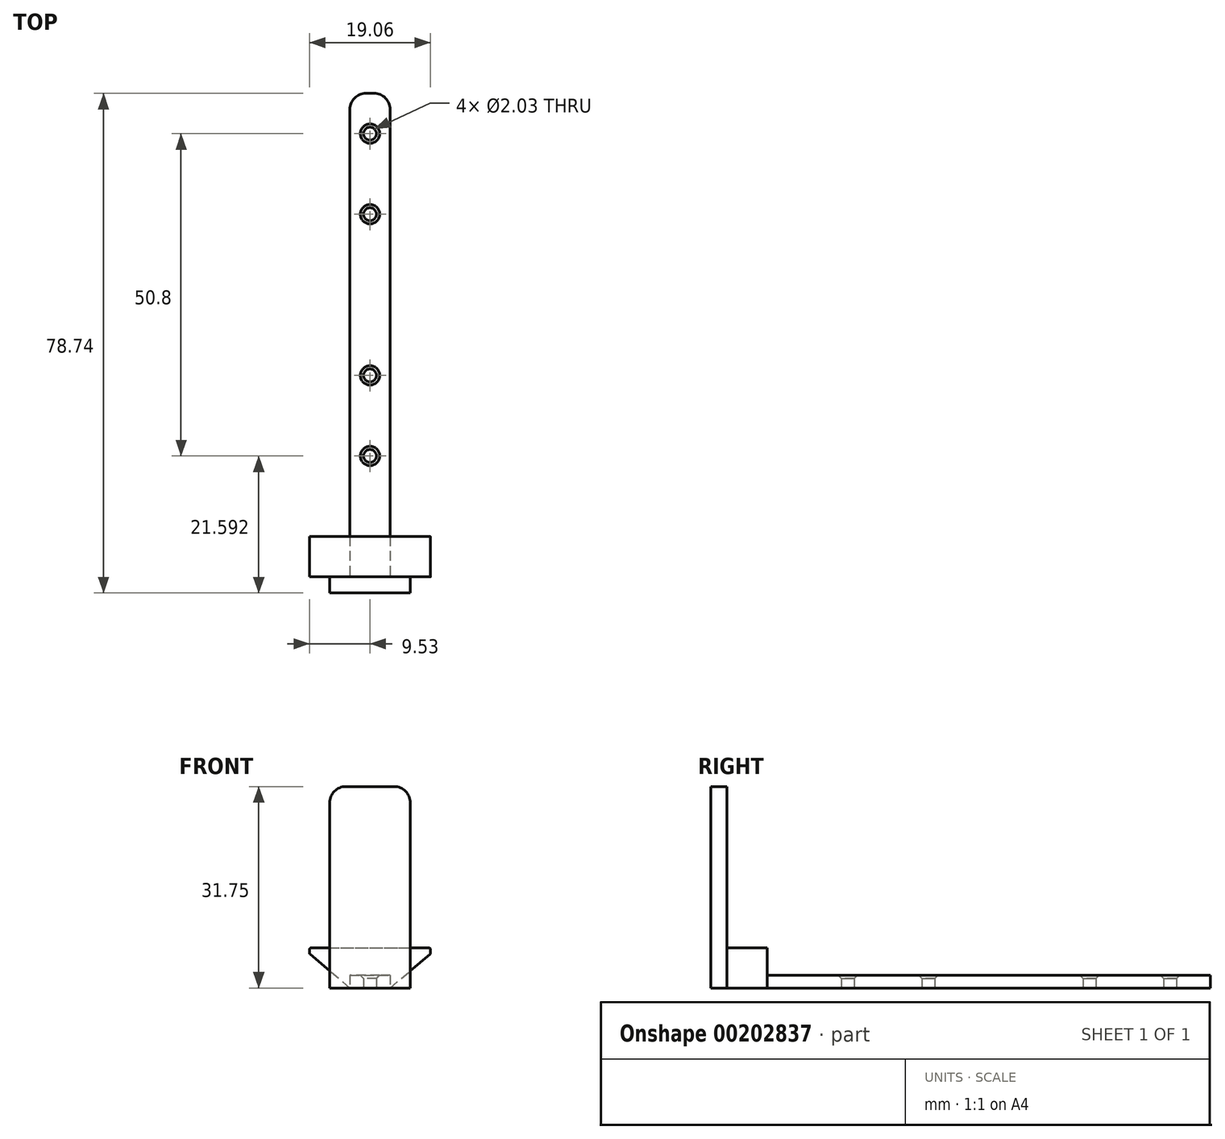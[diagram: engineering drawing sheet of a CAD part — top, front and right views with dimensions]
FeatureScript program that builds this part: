
annotation { "Feature Type Name" : "Feature", "Feature Type Description" : "" }
export const myFeature = defineFeature(function(context is Context, id is Id, definition is map)
    precondition{}
    {
        {
            var Q0;
            Q0=qCreatedBy(makeId("Top.planeOp"),FACE);
            var sketch = newSketch(context, id + "F0", { "sketchPlane" : qUnion([Q0])});
            skLineSegment(sketch, "E0.bottom", {"start": v(-3.18, 67.1) * mm, "end": v(3.18, 67.1) * mm});
            skLineSegment(sketch, "E0.top", {"start": v(-3.18, -9.1) * mm, "end": v(3.18, -9.1) * mm});
            skLineSegment(sketch, "E0.left", {"start": v(-3.18, 67.1) * mm, "end": v(-3.18, -9.1) * mm});
            skLineSegment(sketch, "E0.right", {"start": v(3.18, 67.1) * mm, "end": v(3.18, -9.1) * mm});
            skCircle(sketch, "E1", {"center": v(0, 9.94) * mm, "radius": 1.02 * mm});
            skCircle(sketch, "E2", {"center": v(0, 22.64) * mm, "radius": 1.02 * mm});
            skCircle(sketch, "E3", {"center": v(0, 48.04) * mm, "radius": 1.02 * mm});
            skCircle(sketch, "E4", {"center": v(0, 60.74) * mm, "radius": 1.02 * mm});
            skSolve(sketch);
        }
        {
            var Q0;
            Q0=makeQuery(id+"F0.imprint","IMPRINT",FACE,{"disambiguationData":[TD([[makeQuery(id+"F0.imprint","IMPRINT",EDGE,{"derivedFrom":sQuery(id+"F0.wireOp",EDGE,"E0.bottom")}),-1.0]])]});
            extrude(context, id + "F1", {"entities" : qUnion([Q0]), "depth" : 2.03 * mm});
        }
        {
            var Q0;
            Q0=makeQuery(id+"F1.opExtrude","SWEPT_FACE",FACE,{"disambiguationData":[OSD([sQuery(id+"F0.wireOp",EDGE,"E0.top")])]});
            var sketch = newSketch(context, id + "F2", { "sketchPlane" : qUnion([Q0])});
            skPoint(sketch, "E5.oppositeSnap0", {"position": v(3.17, 1.02) * mm});
            skLineSegment(sketch, "E5.bottom", {"start": v(-3.18, 0) * mm, "end": v(3.17, 0) * mm});
            skLineSegment(sketch, "E5.top", {"start": v(-3.18, 6.35) * mm, "end": v(3.17, 6.35) * mm});
            skLineSegment(sketch, "E6", {"start": v(3.18, 0) * mm, "end": v(9.52, 5.36) * mm});
            skLineSegment(sketch, "E7", {"start": v(-3.18, 0) * mm, "end": v(-9.52, 5.39) * mm});
            skLineSegment(sketch, "E8", {"start": v(-9.53, 6.35) * mm, "end": v(-9.53, 5.39) * mm});
            skLineSegment(sketch, "E9", {"start": v(9.52, 6.35) * mm, "end": v(9.52, 5.36) * mm});
            skLineSegment(sketch, "E10", {"start": v(-9.53, 6.35) * mm, "end": v(9.52, 6.35) * mm});
            skSolve(sketch);
        }
        {
            var Q0;
            Q0 = qSketchRegion(id + "F2", true);
            extrude(context, id + "F3", {"entities" : qUnion([Q0]), "operationType" : NewBodyOperationType.ADD, "oppositeDirection" : true, "depth" : 6.35 * mm});
        }
        {
            var Q0;
            Q0=makeQuery(id+"F3.opExtrude","SWEPT_EDGE",EDGE,{"disambiguationData":[OSD([sQuery(id+"F2.wireOp",EDGE,"E9"),sQuery(id+"F2.wireOp",EDGE,"E10")])]});
            fillet(context, id + "F4", {"entities" : qUnion([Q0]), "radius" : 0.25 * mm, "tangentPropagation" : true, "allowEdgeOverflow" : false});
        }
        {
            var Q0;
            Q0=makeQuery(id+"F3.opExtrude","SWEPT_EDGE",EDGE,{"disambiguationData":[OSD([sQuery(id+"F2.wireOp",EDGE,"E6"),sQuery(id+"F2.wireOp",EDGE,"E9")])]});
            var Q1;
            Q1=makeQuery(id+"F3.opExtrude","SWEPT_EDGE",EDGE,{"disambiguationData":[OSD([sQuery(id+"F2.wireOp",EDGE,"E8"),sQuery(id+"F2.wireOp",EDGE,"E10")])]});
            var Q2;
            Q2=makeQuery(id+"F3.opExtrude","SWEPT_EDGE",EDGE,{"disambiguationData":[OSD([sQuery(id+"F2.wireOp",EDGE,"E7"),sQuery(id+"F2.wireOp",EDGE,"E8")])]});
            fillet(context, id + "F5", {"entities" : qUnion([Q0, Q1, Q2]), "radius" : 0.25 * mm, "tangentPropagation" : true, "allowEdgeOverflow" : false});
        }
        {
            var Q0;
            Q0=makeQuery(id+"F1.opExtrude","CAP_EDGE",EDGE,{"disambiguationData":[OSD([sQuery(id+"F0.wireOp",EDGE,"E4")])],"isStart":false});
            chamfer(context, id + "F6", {"entities" : qUnion([Q0]), "width" : 0.5 * mm, "tangentPropagation" : true});
        }
        {
            var Q0;
            Q0=makeQuery(id+"F1.opExtrude","CAP_EDGE",EDGE,{"disambiguationData":[OSD([sQuery(id+"F0.wireOp",EDGE,"E3")])],"isStart":false});
            var Q1;
            Q1=makeQuery(id+"F1.opExtrude","CAP_EDGE",EDGE,{"disambiguationData":[OSD([sQuery(id+"F0.wireOp",EDGE,"E2")])],"isStart":false});
            var Q2;
            Q2=makeQuery(id+"F1.opExtrude","CAP_EDGE",EDGE,{"disambiguationData":[OSD([sQuery(id+"F0.wireOp",EDGE,"E1")])],"isStart":false});
            chamfer(context, id + "F7", {"entities" : qUnion([Q0, Q1, Q2]), "width" : 0.5 * mm, "tangentPropagation" : true});
        }
        {
            var Q0;
            Q0=makeQuery(id+"F3.boolean.opBoolean","MERGE",FACE,{"derivedFrom":[makeQuery(id+"F1.opExtrude","SWEPT_FACE",FACE,{"disambiguationData":[OSD([sQuery(id+"F0.wireOp",EDGE,"E0.top")])]}),makeQuery(id+"F3.opExtrude","CAP_FACE",FACE,{"disambiguationData":[OSD([sQuery(id+"F2.wireOp",EDGE,"E5.bottom"),sQuery(id+"F2.wireOp",EDGE,"E6"),sQuery(id+"F2.wireOp",EDGE,"E7"),sQuery(id+"F2.wireOp",EDGE,"E8"),sQuery(id+"F2.wireOp",EDGE,"E9"),sQuery(id+"F2.wireOp",EDGE,"E10")])],"isStart":true})]});
            var sketch = newSketch(context, id + "F8", { "sketchPlane" : qUnion([Q0])});
            skLineSegment(sketch, "E11.bottom", {"start": v(-6.35, 31.75) * mm, "end": v(6.35, 31.75) * mm});
            skLineSegment(sketch, "E11.top", {"start": v(-6.35, 0) * mm, "end": v(6.35, 0) * mm});
            skLineSegment(sketch, "E11.left", {"start": v(-6.35, 31.75) * mm, "end": v(-6.35, 0) * mm});
            skLineSegment(sketch, "E11.right", {"start": v(6.35, 31.75) * mm, "end": v(6.35, 0) * mm});
            skSolve(sketch);
        }
        {
            var Q0;
            {var subQ0=sQuery(id+"F8.wireOp",EDGE,"E11.bottom");Q0=makeQuery(id+"F8.imprint","IMPRINT",FACE,{"disambiguationData":[TD([[makeQuery(id+"F8.imprint","IMPRINT",EDGE,{"derivedFrom":subQ0}),-1.0]])]});}
            var Q1;
            {var subQ5=sQuery(id+"F8.wireOp",EDGE,"E11.top");var subQ9=makeQuery(id+"F3.opExtrude","CAP_EDGE",EDGE,{"disambiguationData":[OSD([sQuery(id+"F2.wireOp",EDGE,"E7")])],"isStart":true});var subQ11=makeQuery(id+"F8.imprint","INTERSECT",VERTEX,{"derivedFrom":[subQ9,subQ5]});Q1=makeQuery(id+"F8.imprint","IMPRINT",FACE,{"disambiguationData":[TD([[makeQuery(id+"F8.imprint","IMPRINT",EDGE,{"disambiguationData":[TD([[subQ11,-1.0]])],"derivedFrom":subQ5}),1.0]])]});}
            var Q2;
            {var subQ0=sQuery(id+"F8.wireOp",EDGE,"E11.top");var subQ1=makeQuery(id+"F3.opExtrude","CAP_EDGE",EDGE,{"disambiguationData":[OSD([sQuery(id+"F2.wireOp",EDGE,"E6")])],"isStart":true});var subQ2=makeQuery(id+"F8.imprint","INTERSECT",VERTEX,{"derivedFrom":[subQ1,subQ0]});Q2=makeQuery(id+"F8.imprint","IMPRINT",FACE,{"disambiguationData":[TD([[makeQuery(id+"F8.imprint","IMPRINT",EDGE,{"disambiguationData":[TD([[subQ2,-1.0]])],"derivedFrom":subQ0}),1.0]])]});}
            var Q3;
            {var subQ0=sQuery(id+"F8.wireOp",EDGE,"E11.top");var subQ1=makeQuery(id+"F3.opExtrude","CAP_EDGE",EDGE,{"disambiguationData":[OSD([sQuery(id+"F2.wireOp",EDGE,"E7")])],"isStart":true});var subQ2=makeQuery(id+"F8.imprint","INTERSECT",VERTEX,{"derivedFrom":[subQ1,subQ0]});Q3=makeQuery(id+"F8.imprint","IMPRINT",FACE,{"disambiguationData":[TD([[makeQuery(id+"F8.imprint","IMPRINT",EDGE,{"disambiguationData":[TD([[subQ2,1.0]])],"derivedFrom":subQ0}),1.0]])]});}
            extrude(context, id + "F9", {"entities" : qUnion([Q0, Q1, Q2, Q3]), "operationType" : NewBodyOperationType.ADD, "depth" : 2.54 * mm});
        }
        {
            var Q0;
            Q0=makeQuery(id+"F9.opExtrude","SWEPT_EDGE",EDGE,{"disambiguationData":[OSD([sQuery(id+"F8.wireOp",EDGE,"E11.bottom"),sQuery(id+"F8.wireOp",EDGE,"E11.right")])]});
            var Q1;
            Q1=makeQuery(id+"F9.opExtrude","SWEPT_EDGE",EDGE,{"disambiguationData":[OSD([sQuery(id+"F8.wireOp",EDGE,"E11.bottom"),sQuery(id+"F8.wireOp",EDGE,"E11.left")])]});
            fillet(context, id + "F10", {"entities" : qUnion([Q0, Q1]), "radius" : 2.54 * mm, "tangentPropagation" : true, "allowEdgeOverflow" : false});
        }
        {
            var Q0;
            Q0=makeQuery(id+"F1.opExtrude","SWEPT_EDGE",EDGE,{"disambiguationData":[OSD([sQuery(id+"F0.wireOp",EDGE,"E0.bottom"),sQuery(id+"F0.wireOp",EDGE,"E0.left")])]});
            var Q1;
            Q1=makeQuery(id+"F1.opExtrude","SWEPT_EDGE",EDGE,{"disambiguationData":[OSD([sQuery(id+"F0.wireOp",EDGE,"E0.bottom"),sQuery(id+"F0.wireOp",EDGE,"E0.right")])]});
            fillet(context, id + "F11", {"entities" : qUnion([Q0, Q1]), "radius" : 2.54 * mm, "tangentPropagation" : true, "allowEdgeOverflow" : false});
        }
    });
